# Revit family: Cuba Morgana Compact 48 FX (93815-192)
name_source: partatom
category: Modelos genéricos
units: mm (PartAtom-declared; Revit-internal decimal feet)

## family parameters
Com base no plano de trabalho = Não
Compartilhado = Não
Corte com vazios quando carregada = Não
Cota do conector redondo = Utilizar diâmetro
Pode hospedar o vergalhão = Não
Ponto de cálculo do ambiente = Não
Sempre na vertical = Sim
Tipo de parte = Normal

## types (1)
- Cuba Morgana Compact 48 FX (93815-192)
    Acabamento = Acetinado
    Conteúdo do jogo = 1 Válvula Tramontina Luxo 4 1/2''
    Descrição = Cuba Undermount
    Dimensões = 550 x 420 x 190 mm (profundidade)
    Dimensões do nicho = 525 x 395 mm
    Diâmetro do cano de saída = 34 mm
    Elevação padrão = 0 mm  [stored 0 ft]
    Espessura = 0,8 mm
    Fabricante = Tramontina
    Furação para torneira e misturador de sabão = DIA 35 mm
    Material predominante = Aço Inox
    Modelo = Morgana Compact 48 FX Undermount
    Raio dos cantos do nicho = 15 mm
    Referência do produto = 93806/192
    Tipo de material = AISI 304
    URL do fabricante = tramontina.com.br
    URL do manual do produto = https://assets.tramontina.com.br
    URL do produto = https://www.tramontina.com.br
    URL dos arquivos BIM = tramontina.com.br/biblioteca
    Volume = 25 L

note: [stored X ft] marks values corroborated as IEEE doubles in the binary element streams (Revit-internal decimal feet)
